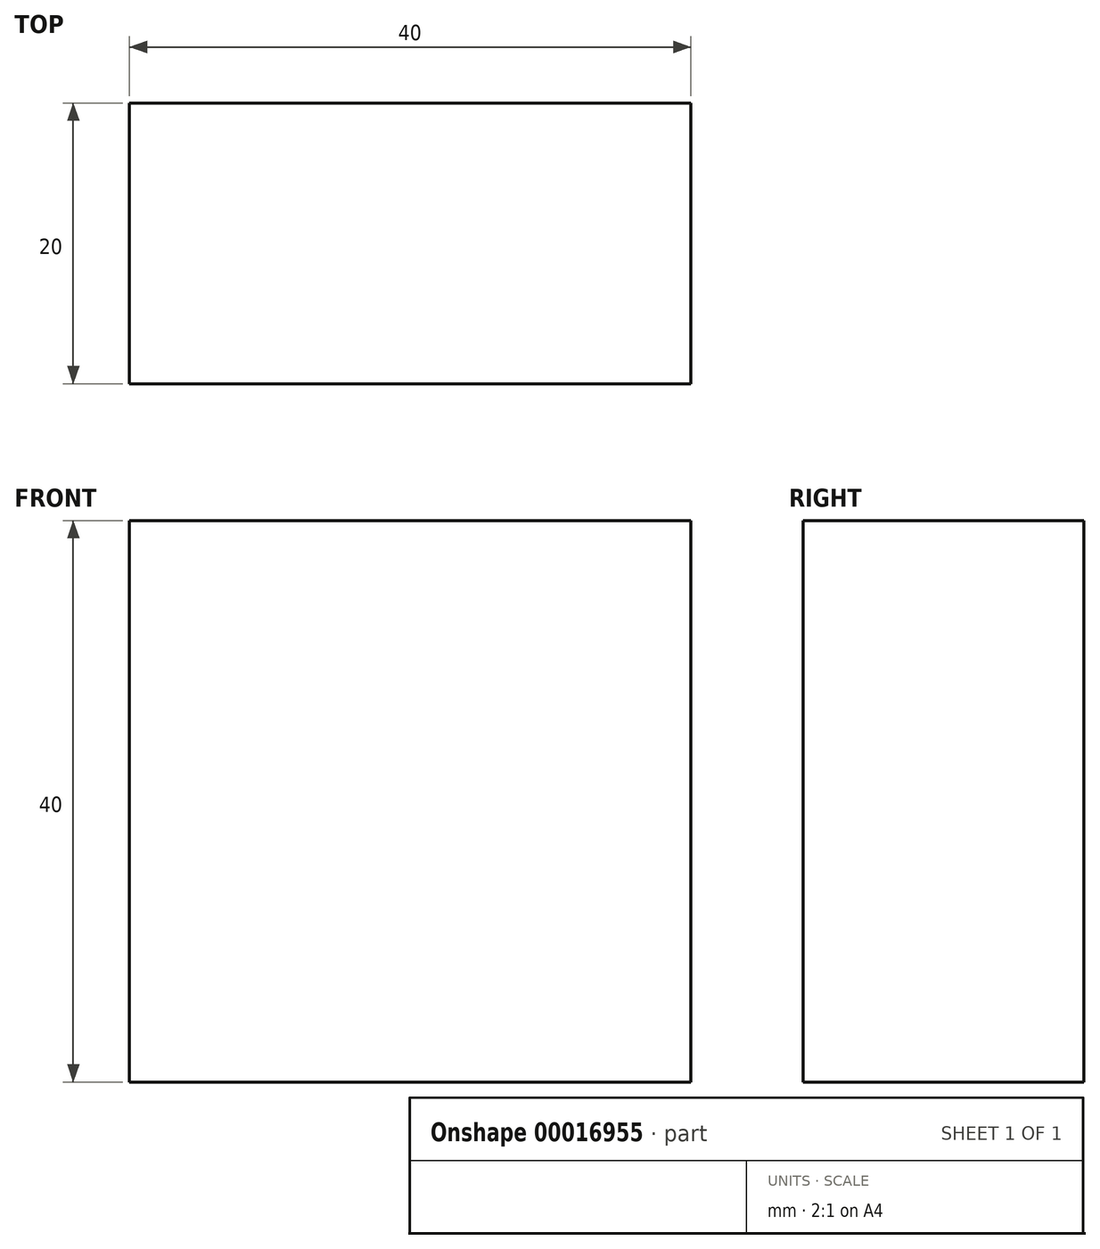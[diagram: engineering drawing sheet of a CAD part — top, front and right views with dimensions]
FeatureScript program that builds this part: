
annotation { "Feature Type Name" : "Feature", "Feature Type Description" : "" }
export const myFeature = defineFeature(function(context is Context, id is Id, definition is map)
    precondition{}
    {
        {
            var Q0;
            Q0=qCreatedBy(makeId("Top.planeOp"),FACE);
            var sketch = newSketch(context, id + "F0", { "sketchPlane" : qUnion([Q0])});
            skLineSegment(sketch, "E0.bottom", {"start": v(-36.19, -39.78) * mm, "end": v(3.81, -39.78) * mm});
            skLineSegment(sketch, "E0.top", {"start": v(-36.19, -19.78) * mm, "end": v(3.81, -19.78) * mm});
            skLineSegment(sketch, "E0.left", {"start": v(-36.19, -39.78) * mm, "end": v(-36.19, -19.78) * mm});
            skLineSegment(sketch, "E0.right", {"start": v(3.81, -39.78) * mm, "end": v(3.81, -19.78) * mm});
            skSolve(sketch);
        }
        {
            var Q0;
            Q0 = qSketchRegion(id + "F0", true);
            extrude(context, id + "F1", {"entities" : qUnion([Q0]), "depth" : 40 * mm});
        }
    });
